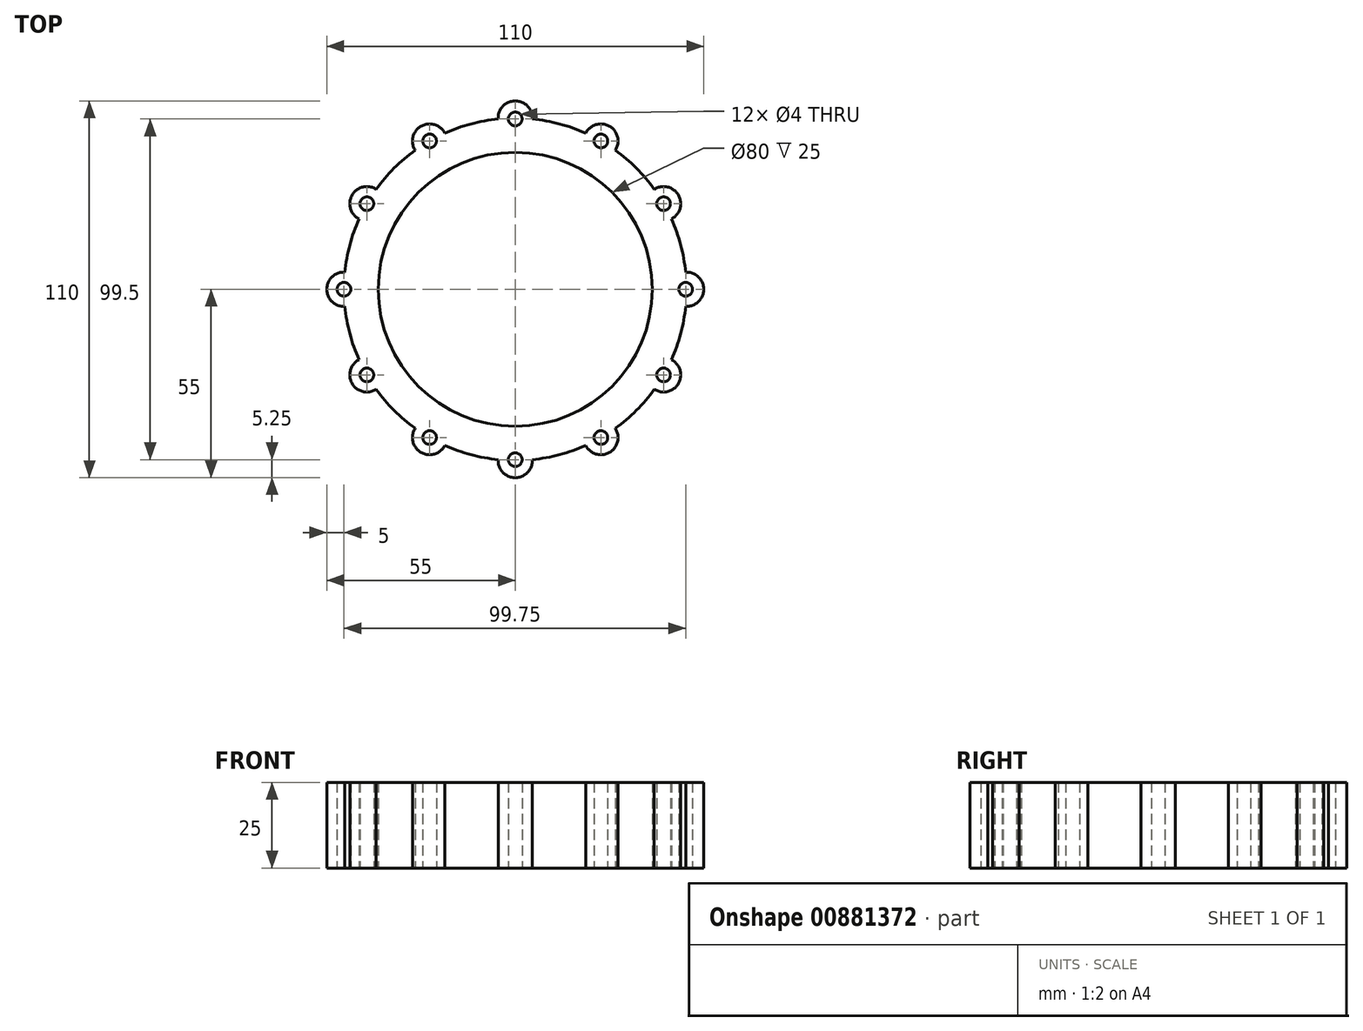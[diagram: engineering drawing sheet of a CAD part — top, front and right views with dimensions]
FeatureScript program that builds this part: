
annotation { "Feature Type Name" : "Feature", "Feature Type Description" : "" }
export const myFeature = defineFeature(function(context is Context, id is Id, definition is map)
    precondition{}
    {
        {
            var Q0;
            Q0=qCreatedBy(makeId("Top.planeOp"),FACE);
            var sketch = newSketch(context, id + "F0", { "sketchPlane" : qUnion([Q0])});
            skCircle(sketch, "E0", {"center": v(0, 0) * mm, "radius": 50 * mm});
            skCircle(sketch, "E1", {"center": v(0, 50) * mm, "radius": 5 * mm});
            skSolve(sketch);
        }
        {
            var Q0;
            {var subQ0=sQuery(id+"F0.wireOp",EDGE,"E1");var subQ1=sQuery(id+"F0.wireOp",EDGE,"E0");var subQ2=makeQuery(id+"F0.imprint","INTERSECT",VERTEX,{"disambiguationData":[OD(0.0)],"derivedFrom":[subQ1,subQ0]});Q0=makeQuery(id+"F0.imprint","IMPRINT",FACE,{"disambiguationData":[TD([[makeQuery(id+"F0.imprint","IMPRINT",EDGE,{"disambiguationData":[TD([[subQ2,-1.0]])],"derivedFrom":subQ1}),1.0]])]});}
            var Q1;
            {var subQ0=sQuery(id+"F0.wireOp",EDGE,"E1");var subQ1=sQuery(id+"F0.wireOp",EDGE,"E0");var subQ2=makeQuery(id+"F0.imprint","INTERSECT",VERTEX,{"disambiguationData":[OD(0.0)],"derivedFrom":[subQ1,subQ0]});Q1=makeQuery(id+"F0.imprint","IMPRINT",FACE,{"disambiguationData":[TD([[makeQuery(id+"F0.imprint","IMPRINT",EDGE,{"disambiguationData":[TD([[subQ2,1.0]])],"derivedFrom":subQ1}),1.0]])]});}
            var Q2;
            {var subQ0=sQuery(id+"F0.wireOp",EDGE,"E1");var subQ1=sQuery(id+"F0.wireOp",EDGE,"E0");var subQ2=makeQuery(id+"F0.imprint","INTERSECT",VERTEX,{"disambiguationData":[OD(0.0)],"derivedFrom":[subQ1,subQ0]});Q2=makeQuery(id+"F0.imprint","IMPRINT",FACE,{"disambiguationData":[TD([[makeQuery(id+"F0.imprint","IMPRINT",EDGE,{"disambiguationData":[TD([[subQ2,1.0]])],"derivedFrom":subQ1}),-1.0]])]});}
            extrude(context, id + "F1", {"entities" : qUnion([Q0, Q1, Q2]), "depth" : 25 * mm, "offsetDistance" : 25 * mm});
        }
        {
            var Q0;
            Q0=makeQuery(id+"F1.opExtrude","SWEPT_BODY",BODY,{"disambiguationData":[OSD([sQuery(id+"F0.wireOp",EDGE,"E0"),sQuery(id+"F0.wireOp",EDGE,"E1")])]});
            var Q1;
            Q1=makeQuery(id+"F1.opExtrude","SWEPT_FACE",FACE,{"disambiguationData":[OSD([sQuery(id+"F0.wireOp",EDGE,"E0")])]});
            circularPattern(context, id + "F2", {"entities" : qUnion([Q0]), "axis" : qUnion([Q1]), "angle" : 360 * degree, "instanceCount" : 12, "equalSpace" : true});
        }
        {
            var Q0;
            Q0=makeQuery(id+"F1.opExtrude","SWEPT_BODY",BODY,{"disambiguationData":[OSD([sQuery(id+"F0.wireOp",EDGE,"E0"),sQuery(id+"F0.wireOp",EDGE,"E1")])]});
            var Q1;
            Q1=makeQuery(id+"F2.opPattern","COPY",BODY,{"derivedFrom":makeQuery(id+"F1.opExtrude","SWEPT_BODY",BODY,{"disambiguationData":[OSD([sQuery(id+"F0.wireOp",EDGE,"E0"),sQuery(id+"F0.wireOp",EDGE,"E1")])]}),"instanceName":"5"});
            var Q2;
            Q2=makeQuery(id+"F2.opPattern","COPY",BODY,{"derivedFrom":makeQuery(id+"F1.opExtrude","SWEPT_BODY",BODY,{"disambiguationData":[OSD([sQuery(id+"F0.wireOp",EDGE,"E0"),sQuery(id+"F0.wireOp",EDGE,"E1")])]}),"instanceName":"6"});
            var Q3;
            Q3=makeQuery(id+"F2.opPattern","COPY",BODY,{"derivedFrom":makeQuery(id+"F1.opExtrude","SWEPT_BODY",BODY,{"disambiguationData":[OSD([sQuery(id+"F0.wireOp",EDGE,"E0"),sQuery(id+"F0.wireOp",EDGE,"E1")])]}),"instanceName":"1"});
            var Q4;
            Q4=makeQuery(id+"F2.opPattern","COPY",BODY,{"derivedFrom":makeQuery(id+"F1.opExtrude","SWEPT_BODY",BODY,{"disambiguationData":[OSD([sQuery(id+"F0.wireOp",EDGE,"E0"),sQuery(id+"F0.wireOp",EDGE,"E1")])]}),"instanceName":"2"});
            var Q5;
            Q5=makeQuery(id+"F2.opPattern","COPY",BODY,{"derivedFrom":makeQuery(id+"F1.opExtrude","SWEPT_BODY",BODY,{"disambiguationData":[OSD([sQuery(id+"F0.wireOp",EDGE,"E0"),sQuery(id+"F0.wireOp",EDGE,"E1")])]}),"instanceName":"3"});
            var Q6;
            Q6=makeQuery(id+"F2.opPattern","COPY",BODY,{"derivedFrom":makeQuery(id+"F1.opExtrude","SWEPT_BODY",BODY,{"disambiguationData":[OSD([sQuery(id+"F0.wireOp",EDGE,"E0"),sQuery(id+"F0.wireOp",EDGE,"E1")])]}),"instanceName":"4"});
            var Q7;
            Q7=makeQuery(id+"F2.opPattern","COPY",BODY,{"derivedFrom":makeQuery(id+"F1.opExtrude","SWEPT_BODY",BODY,{"disambiguationData":[OSD([sQuery(id+"F0.wireOp",EDGE,"E0"),sQuery(id+"F0.wireOp",EDGE,"E1")])]}),"instanceName":"11"});
            var Q8;
            Q8=makeQuery(id+"F2.opPattern","COPY",BODY,{"derivedFrom":makeQuery(id+"F1.opExtrude","SWEPT_BODY",BODY,{"disambiguationData":[OSD([sQuery(id+"F0.wireOp",EDGE,"E0"),sQuery(id+"F0.wireOp",EDGE,"E1")])]}),"instanceName":"10"});
            var Q9;
            Q9=makeQuery(id+"F2.opPattern","COPY",BODY,{"derivedFrom":makeQuery(id+"F1.opExtrude","SWEPT_BODY",BODY,{"disambiguationData":[OSD([sQuery(id+"F0.wireOp",EDGE,"E0"),sQuery(id+"F0.wireOp",EDGE,"E1")])]}),"instanceName":"7"});
            var Q10;
            Q10=makeQuery(id+"F2.opPattern","COPY",BODY,{"derivedFrom":makeQuery(id+"F1.opExtrude","SWEPT_BODY",BODY,{"disambiguationData":[OSD([sQuery(id+"F0.wireOp",EDGE,"E0"),sQuery(id+"F0.wireOp",EDGE,"E1")])]}),"instanceName":"8"});
            var Q11;
            Q11=makeQuery(id+"F2.opPattern","COPY",BODY,{"derivedFrom":makeQuery(id+"F1.opExtrude","SWEPT_BODY",BODY,{"disambiguationData":[OSD([sQuery(id+"F0.wireOp",EDGE,"E0"),sQuery(id+"F0.wireOp",EDGE,"E1")])]}),"instanceName":"9"});
            booleanBodies(context, id + "F3", {"operationType" : BooleanOperationType.UNION, "tools" : qUnion([Q0, Q1, Q2, Q3, Q4, Q5, Q6, Q7, Q8, Q9, Q10, Q11])});
        }
        {
            var Q0;
            {var subQ0=makeQuery(id+"F1.opExtrude","CAP_FACE",FACE,{"disambiguationData":[OSD([sQuery(id+"F0.wireOp",EDGE,"E0"),sQuery(id+"F0.wireOp",EDGE,"E1")])],"isStart":true});Q0=makeQuery(id+"F3.opBoolean","MERGE",FACE,{"derivedFrom":[subQ0,makeQuery(id+"F2.opPattern","COPY",FACE,{"derivedFrom":subQ0,"instanceName":"1"}),makeQuery(id+"F2.opPattern","COPY",FACE,{"derivedFrom":subQ0,"instanceName":"2"}),makeQuery(id+"F2.opPattern","COPY",FACE,{"derivedFrom":subQ0,"instanceName":"3"}),makeQuery(id+"F2.opPattern","COPY",FACE,{"derivedFrom":subQ0,"instanceName":"4"}),makeQuery(id+"F2.opPattern","COPY",FACE,{"derivedFrom":subQ0,"instanceName":"5"}),makeQuery(id+"F2.opPattern","COPY",FACE,{"derivedFrom":subQ0,"instanceName":"6"}),makeQuery(id+"F2.opPattern","COPY",FACE,{"derivedFrom":subQ0,"instanceName":"7"}),makeQuery(id+"F2.opPattern","COPY",FACE,{"derivedFrom":subQ0,"instanceName":"8"}),makeQuery(id+"F2.opPattern","COPY",FACE,{"derivedFrom":subQ0,"instanceName":"9"}),makeQuery(id+"F2.opPattern","COPY",FACE,{"derivedFrom":subQ0,"instanceName":"10"}),makeQuery(id+"F2.opPattern","COPY",FACE,{"derivedFrom":subQ0,"instanceName":"11"})]});}
            var sketch = newSketch(context, id + "F4", { "sketchPlane" : qUnion([Q0])});
            skPoint(sketch, "E2", {"position": v(25, -43.3) * mm});
            skPoint(sketch, "E3", {"position": v(-25, -43.3) * mm});
            skPoint(sketch, "E4", {"position": v(-50, 0) * mm});
            skPoint(sketch, "E5", {"position": v(-43.3, -25) * mm});
            skPoint(sketch, "E6", {"position": v(43.3, -25) * mm});
            skPoint(sketch, "E7", {"position": v(49.75, 0) * mm});
            skPoint(sketch, "E7.positionSnap0", {"position": v(55, 0) * mm});
            skPoint(sketch, "E8", {"position": v(43.3, 25) * mm});
            skPoint(sketch, "E9", {"position": v(25, 43.3) * mm});
            skPoint(sketch, "E10.positionSnap0", {"position": v(12.94, 48.3) * mm});
            skPoint(sketch, "E11", {"position": v(0, 49.75) * mm});
            skPoint(sketch, "E12", {"position": v(-25, 43.3) * mm});
            skPoint(sketch, "E13", {"position": v(-43.3, 25) * mm});
            skPoint(sketch, "E14", {"position": v(0, -49.75) * mm});
            skPoint(sketch, "E14.positionSnap0", {"position": v(0, -55) * mm});
            skSolve(sketch);
        }
        {
            var Q0;
            Q0=sQuery(id+"F4.wireOp",VERTEX,"E6");
            var Q1;
            Q1=sQuery(id+"F4.wireOp",VERTEX,"E2");
            var Q2;
            Q2=sQuery(id+"F4.wireOp",VERTEX,"E14");
            var Q3;
            Q3=sQuery(id+"F4.wireOp",VERTEX,"E3");
            var Q4;
            Q4=sQuery(id+"F4.wireOp",VERTEX,"E5");
            var Q5;
            Q5=sQuery(id+"F4.wireOp",VERTEX,"E4");
            var Q6;
            Q6=sQuery(id+"F4.wireOp",VERTEX,"E13");
            var Q7;
            Q7=sQuery(id+"F4.wireOp",VERTEX,"E12");
            var Q8;
            Q8=sQuery(id+"F4.wireOp",VERTEX,"E11");
            var Q9;
            Q9=sQuery(id+"F4.wireOp",VERTEX,"E9");
            var Q10;
            Q10=sQuery(id+"F4.wireOp",VERTEX,"E8");
            var Q11;
            Q11=sQuery(id+"F4.wireOp",VERTEX,"E7");
            var Q12;
            Q12=makeQuery(id+"F1.opExtrude","SWEPT_BODY",BODY,{"disambiguationData":[OSD([sQuery(id+"F0.wireOp",EDGE,"E0"),sQuery(id+"F0.wireOp",EDGE,"E1")])]});
            hole(context, id + "F5", {"style" : HoleStyle.SIMPLE, "endStyle" : HoleEndStyle.THROUGH, "holeDiameter" : 4 * mm, "majorDiameter" : 5 * mm, "isTappedThrough" : true, "tappedDepth" : 12 * mm, "tapClearance" : 3, "locations" : qUnion([Q0, Q1, Q2, Q3, Q4, Q5, Q6, Q7, Q8, Q9, Q10, Q11]), "scope" : qUnion([Q12])});
        }
        {
            var Q0;
            {var subQ0=makeQuery(id+"F1.opExtrude","CAP_FACE",FACE,{"disambiguationData":[OSD([sQuery(id+"F0.wireOp",EDGE,"E0"),sQuery(id+"F0.wireOp",EDGE,"E1")])],"isStart":true});Q0=makeQuery(id+"F3.opBoolean","MERGE",FACE,{"derivedFrom":[subQ0,makeQuery(id+"F2.opPattern","COPY",FACE,{"derivedFrom":subQ0,"instanceName":"1"}),makeQuery(id+"F2.opPattern","COPY",FACE,{"derivedFrom":subQ0,"instanceName":"2"}),makeQuery(id+"F2.opPattern","COPY",FACE,{"derivedFrom":subQ0,"instanceName":"3"}),makeQuery(id+"F2.opPattern","COPY",FACE,{"derivedFrom":subQ0,"instanceName":"4"}),makeQuery(id+"F2.opPattern","COPY",FACE,{"derivedFrom":subQ0,"instanceName":"5"}),makeQuery(id+"F2.opPattern","COPY",FACE,{"derivedFrom":subQ0,"instanceName":"6"}),makeQuery(id+"F2.opPattern","COPY",FACE,{"derivedFrom":subQ0,"instanceName":"7"}),makeQuery(id+"F2.opPattern","COPY",FACE,{"derivedFrom":subQ0,"instanceName":"8"}),makeQuery(id+"F2.opPattern","COPY",FACE,{"derivedFrom":subQ0,"instanceName":"9"}),makeQuery(id+"F2.opPattern","COPY",FACE,{"derivedFrom":subQ0,"instanceName":"10"}),makeQuery(id+"F2.opPattern","COPY",FACE,{"derivedFrom":subQ0,"instanceName":"11"})]});}
            var sketch = newSketch(context, id + "F6", { "sketchPlane" : qUnion([Q0])});
            skCircle(sketch, "E15", {"center": v(0, 0) * mm, "radius": 40 * mm});
            skSolve(sketch);
        }
        {
            var Q0;
            Q0=makeQuery(id+"F6.imprint","IMPRINT",FACE,{"disambiguationData":[TD([[makeQuery(id+"F6.imprint","IMPRINT",EDGE,{"derivedFrom":sQuery(id+"F6.wireOp",EDGE,"E15")}),1.0]])]});
            extrude(context, id + "F7", {"entities" : qUnion([Q0]), "operationType" : NewBodyOperationType.REMOVE, "endBound" : BoundingType.THROUGH_ALL, "oppositeDirection" : true, "depth" : 25 * mm, "offsetDistance" : 25 * mm});
        }
    });
